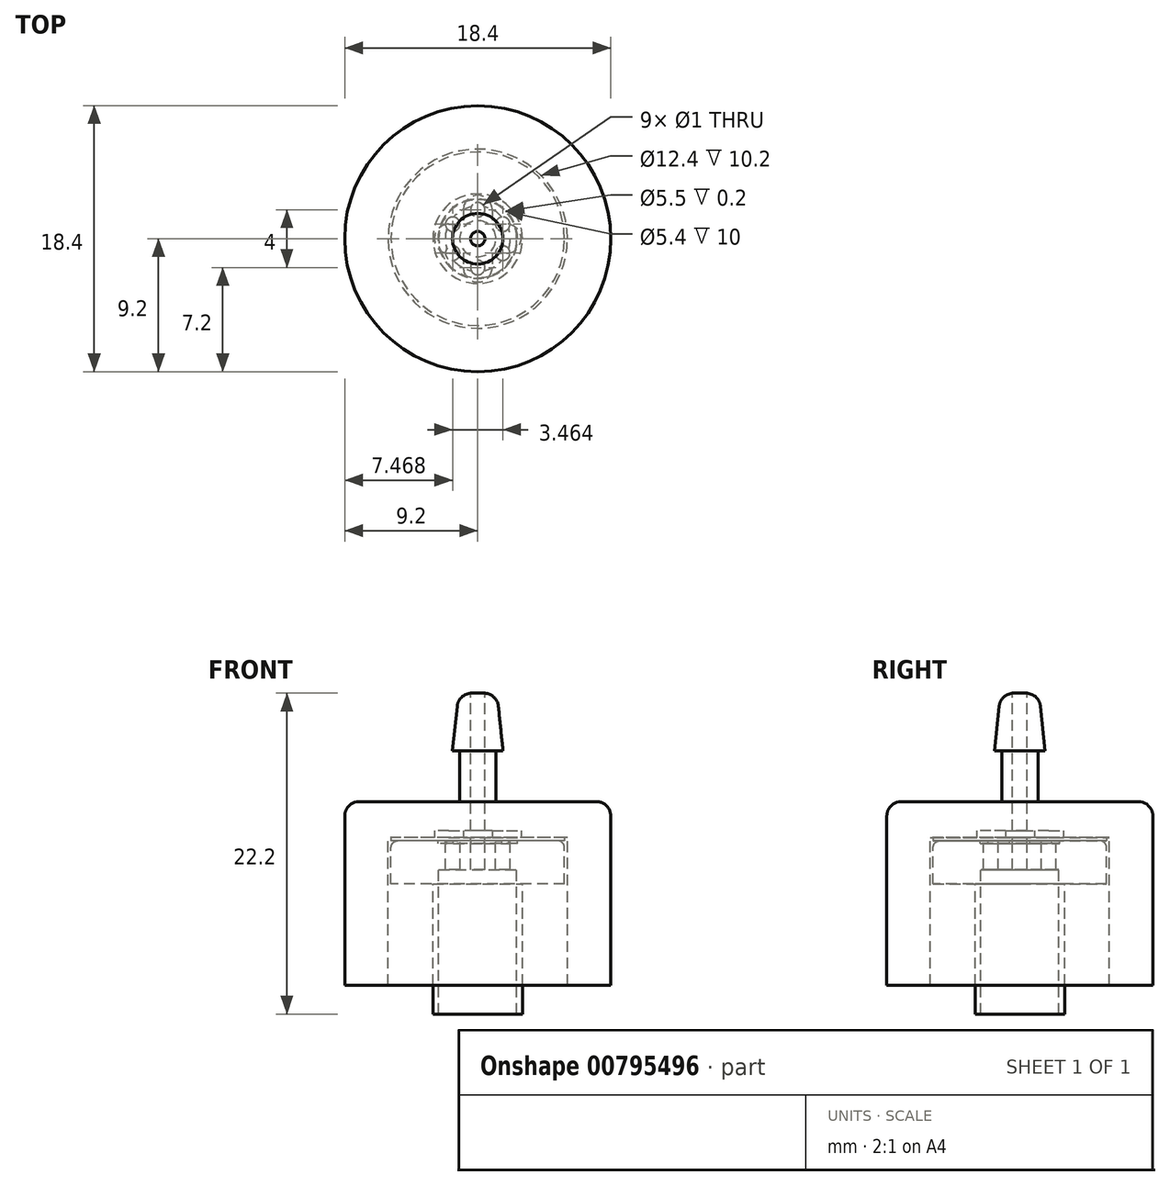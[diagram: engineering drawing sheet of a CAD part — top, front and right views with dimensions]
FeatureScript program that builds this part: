
annotation { "Feature Type Name" : "Feature", "Feature Type Description" : "" }
export const myFeature = defineFeature(function(context is Context, id is Id, definition is map)
    precondition{}
    {
        {
            var Q0;
            Q0=qCreatedBy(makeId("Top.planeOp"),FACE);
            var sketch = newSketch(context, id + "F0", { "sketchPlane" : qUnion([Q0])});
            skCircle(sketch, "E0", {"center": v(0, 0) * mm, "radius": 6 * mm});
            skCircle(sketch, "E1", {"center": v(0, 0) * mm, "radius": 3.1 * mm});
            skCircle(sketch, "E2", {"center": v(0, 2) * mm, "radius": 0.5 * mm});
            skCircle(sketch, "E3.1.0", {"center": v(-1.73, 1) * mm, "radius": 0.5 * mm});
            skCircle(sketch, "E3.2.0", {"center": v(-1.73, -1) * mm, "radius": 0.5 * mm});
            skCircle(sketch, "E3.3.0", {"center": v(0, -2) * mm, "radius": 0.5 * mm});
            skCircle(sketch, "E3.4.0", {"center": v(1.73, -1) * mm, "radius": 0.5 * mm});
            skCircle(sketch, "E3.5.0", {"center": v(1.73, 1) * mm, "radius": 0.5 * mm});
            skCircle(sketch, "E4", {"center": v(0, 0) * mm, "radius": 0.5 * mm});
            skSolve(sketch);
        }
        {
            var Q0;
            Q0=makeQuery(id+"F0.imprint","IMPRINT",FACE,{"disambiguationData":[TD([[makeQuery(id+"F0.imprint","IMPRINT",EDGE,{"derivedFrom":sQuery(id+"F0.wireOp",EDGE,"E0")}),1.0]])]});
            var Q1;
            Q1=makeQuery(id+"F0.imprint","IMPRINT",FACE,{"disambiguationData":[TD([[makeQuery(id+"F0.imprint","IMPRINT",EDGE,{"derivedFrom":sQuery(id+"F0.wireOp",EDGE,"E1")}),1.0]])]});
            extrude(context, id + "F1", {"entities" : qUnion([Q0, Q1]), "oppositeDirection" : true, "depth" : 2 * mm, "offsetDistance" : 25 * mm});
        }
        {
            var Q0;
            Q0=makeQuery(id+"F1.opExtrude","CAP_FACE",FACE,{"disambiguationData":[OSD([sQuery(id+"F0.wireOp",EDGE,"E0"),sQuery(id+"F0.wireOp",EDGE,"E2"),sQuery(id+"F0.wireOp",EDGE,"E3.1.0"),sQuery(id+"F0.wireOp",EDGE,"E3.2.0"),sQuery(id+"F0.wireOp",EDGE,"E3.3.0"),sQuery(id+"F0.wireOp",EDGE,"E3.4.0"),sQuery(id+"F0.wireOp",EDGE,"E3.5.0"),sQuery(id+"F0.wireOp",EDGE,"E4")])],"isStart":true});
            var sketch = newSketch(context, id + "F2", { "sketchPlane" : qUnion([Q0])});
            skCircle(sketch, "E5", {"center": v(0, 0) * mm, "radius": 2.75 * mm});
            skCircle(sketch, "E6", {"center": v(0, 0) * mm, "radius": 2.25 * mm});
            skSolve(sketch);
        }
        {
            var Q0;
            Q0=makeQuery(id+"F2.imprint","IMPRINT",FACE,{"disambiguationData":[TD([[makeQuery(id+"F2.imprint","IMPRINT",EDGE,{"derivedFrom":sQuery(id+"F2.wireOp",EDGE,"E5")}),1.0]])]});
            extrude(context, id + "F3", {"entities" : qUnion([Q0]), "operationType" : NewBodyOperationType.REMOVE, "oppositeDirection" : true, "depth" : 0.2 * mm, "offsetDistance" : 25 * mm});
        }
        {
            var Q0;
            Q0=makeQuery(id+"F1.opExtrude","CAP_FACE",FACE,{"disambiguationData":[OSD([sQuery(id+"F0.wireOp",EDGE,"E0")])],"isStart":false});
            var sketch = newSketch(context, id + "F4", { "sketchPlane" : qUnion([Q0])});
            skCircle(sketch, "E7.0", {"center": v(0, 0) * mm, "radius": 3.1 * mm});
            skCircle(sketch, "E7.1", {"center": v(0, 0) * mm, "radius": 6 * mm});
            skCircle(sketch, "E8", {"center": v(0, 0) * mm, "radius": 2.7 * mm});
            skSolve(sketch);
        }
        {
            var Q0;
            Q0=makeQuery(id+"F4.imprint","IMPRINT",FACE,{"disambiguationData":[TD([[makeQuery(id+"F4.imprint","IMPRINT",EDGE,{"derivedFrom":sQuery(id+"F4.wireOp",EDGE,"E7.0")}),-1.0]])]});
            extrude(context, id + "F5", {"entities" : qUnion([Q0]), "operationType" : NewBodyOperationType.ADD, "depth" : 1 * mm, "offsetDistance" : 25 * mm});
        }
        {
            var Q0;
            Q0=makeQuery(id+"F4.imprint","IMPRINT",FACE,{"disambiguationData":[TD([[makeQuery(id+"F4.imprint","IMPRINT",EDGE,{"derivedFrom":sQuery(id+"F4.wireOp",EDGE,"E7.0")}),1.0]])]});
            extrude(context, id + "F6", {"entities" : qUnion([Q0]), "operationType" : NewBodyOperationType.ADD, "depth" : 10 * mm, "offsetDistance" : 25 * mm});
        }
        {
            var Q0;
            Q0=makeQuery(id+"F0.imprint","IMPRINT",FACE,{"disambiguationData":[TD([[makeQuery(id+"F0.imprint","IMPRINT",EDGE,{"derivedFrom":sQuery(id+"F0.wireOp",EDGE,"E0")}),1.0]])]});
            cPlane(context, id + "F7", {"entities" : qUnion([Q0]), "cplaneType" : CPlaneType.OFFSET, "offset" : 0 * mm, "width" : 150 * mm, "height" : 150 * mm});
        }
        {
            var Q0;
            Q0=qCreatedBy(id+"F7.planeOp",FACE);
            var sketch = newSketch(context, id + "F8", { "sketchPlane" : qUnion([Q0])});
            skCircle(sketch, "E9", {"center": v(0, 0) * mm, "radius": 6.2 * mm});
            skCircle(sketch, "E10", {"center": v(0, 0) * mm, "radius": 9.2 * mm});
            skCircle(sketch, "E11.0", {"center": v(-1.73, 1) * mm, "radius": 0.5 * mm});
            skCircle(sketch, "E11.1", {"center": v(0, 2) * mm, "radius": 0.5 * mm});
            skCircle(sketch, "E11.2", {"center": v(1.73, 1) * mm, "radius": 0.5 * mm});
            skCircle(sketch, "E11.3", {"center": v(1.73, -1) * mm, "radius": 0.5 * mm});
            skCircle(sketch, "E11.4", {"center": v(0, -2) * mm, "radius": 0.5 * mm});
            skCircle(sketch, "E11.5", {"center": v(-1.73, -1) * mm, "radius": 0.5 * mm});
            skCircle(sketch, "E11.6", {"center": v(0, 0) * mm, "radius": 0.5 * mm});
            skCircle(sketch, "E12.0", {"center": v(0, 0) * mm, "radius": 6 * mm});
            skSolve(sketch);
        }
        {
            var Q0;
            Q0=makeQuery(id+"F8.imprint","IMPRINT",FACE,{"disambiguationData":[TD([[makeQuery(id+"F8.imprint","IMPRINT",EDGE,{"derivedFrom":sQuery(id+"F8.wireOp",EDGE,"E11.0")}),-1.0]])]});
            var Q1;
            Q1=makeQuery(id+"F8.imprint","IMPRINT",FACE,{"disambiguationData":[TD([[makeQuery(id+"F8.imprint","IMPRINT",EDGE,{"derivedFrom":sQuery(id+"F8.wireOp",EDGE,"E11.0")}),1.0]])]});
            var Q2;
            Q2=makeQuery(id+"F8.imprint","IMPRINT",FACE,{"disambiguationData":[TD([[makeQuery(id+"F8.imprint","IMPRINT",EDGE,{"derivedFrom":sQuery(id+"F8.wireOp",EDGE,"E11.1")}),1.0]])]});
            var Q3;
            Q3=makeQuery(id+"F8.imprint","IMPRINT",FACE,{"disambiguationData":[TD([[makeQuery(id+"F8.imprint","IMPRINT",EDGE,{"derivedFrom":sQuery(id+"F8.wireOp",EDGE,"E11.2")}),1.0]])]});
            var Q4;
            Q4=makeQuery(id+"F8.imprint","IMPRINT",FACE,{"disambiguationData":[TD([[makeQuery(id+"F8.imprint","IMPRINT",EDGE,{"derivedFrom":sQuery(id+"F8.wireOp",EDGE,"E11.3")}),1.0]])]});
            var Q5;
            Q5=makeQuery(id+"F8.imprint","IMPRINT",FACE,{"disambiguationData":[TD([[makeQuery(id+"F8.imprint","IMPRINT",EDGE,{"derivedFrom":sQuery(id+"F8.wireOp",EDGE,"E11.4")}),1.0]])]});
            var Q6;
            Q6=makeQuery(id+"F8.imprint","IMPRINT",FACE,{"disambiguationData":[TD([[makeQuery(id+"F8.imprint","IMPRINT",EDGE,{"derivedFrom":sQuery(id+"F8.wireOp",EDGE,"E11.5")}),1.0]])]});
            var Q7;
            Q7=makeQuery(id+"F8.imprint","IMPRINT",FACE,{"disambiguationData":[TD([[makeQuery(id+"F8.imprint","IMPRINT",EDGE,{"derivedFrom":sQuery(id+"F8.wireOp",EDGE,"E11.6")}),1.0]])]});
            extrude(context, id + "F9", {"entities" : qUnion([Q0, Q1, Q2, Q3, Q4, Q5, Q6, Q7]), "depth" : 0.2 * mm, "offsetDistance" : 25 * mm});
        }
        {
            var Q0;
            Q0 = qSketchRegion(id + "F8", true);
            extrude(context, id + "F10", {"entities" : qUnion([Q0]), "oppositeDirection" : true, "depth" : 10 * mm, "offsetDistance" : 25 * mm});
        }
        {
            var Q0;
            Q0=makeQuery(id+"F10.opExtrude","CAP_FACE",FACE,{"disambiguationData":[OSD([sQuery(id+"F8.wireOp",EDGE,"E9"),sQuery(id+"F8.wireOp",EDGE,"E10")])],"isStart":true});
            extrude(context, id + "F11", {"entities" : qUnion([Q0]), "operationType" : NewBodyOperationType.ADD, "depth" : 0.2 * mm, "offsetDistance" : 25 * mm});
        }
        {
            var Q0;
            Q0=makeQuery(id+"F11.opExtrude","CAP_FACE",FACE,{"disambiguationData":[OSD([sQuery(id+"F8.wireOp",EDGE,"E9"),sQuery(id+"F8.wireOp",EDGE,"E10")])],"isStart":false});
            var sketch = newSketch(context, id + "F12", { "sketchPlane" : qUnion([Q0])});
            skLineSegment(sketch, "E13.bottom", {"start": v(-2, 1) * mm, "end": v(2, 1) * mm});
            skLineSegment(sketch, "E13.top", {"start": v(-2, -1) * mm, "end": v(2, -1) * mm});
            skLineSegment(sketch, "E13.left", {"start": v(-3, 0) * mm, "end": v(-3, 0) * mm});
            skLineSegment(sketch, "E13.right", {"start": v(3, 0) * mm, "end": v(3, 0) * mm});
            skLineSegment(sketch, "E14.bottom", {"start": v(0, 3) * mm, "end": v(0, 3) * mm});
            skLineSegment(sketch, "E14.top", {"start": v(0, -3) * mm, "end": v(0, -3) * mm});
            skLineSegment(sketch, "E14.left", {"start": v(-1, 2) * mm, "end": v(-1, -2) * mm});
            skLineSegment(sketch, "E14.right", {"start": v(1, 2) * mm, "end": v(1, -2) * mm});
            skLineSegment(sketch, "E15", {"start": v(-4.57, 0) * mm, "end": v(4.82, 0) * mm, "construction": true});
            skLineSegment(sketch, "E16", {"start": v(0, 3.73) * mm, "end": v(0, -3.96) * mm, "construction": true});
            skPoint(sketch, "E17.visualSharp", {"position": v(-3, -1) * mm});
            skArc(sketch, "E17.filletArc", {"start": v(-3, 0) * mm, "mid": v(-2.7, -0.7) * mm, "end": v(-2, -1) * mm});
            skPoint(sketch, "E18.visualSharp", {"position": v(-3, 1) * mm});
            skArc(sketch, "E18.filletArc", {"start": v(-2, 1) * mm, "mid": v(-2.7, 0.7) * mm, "end": v(-3, 0) * mm});
            skPoint(sketch, "E19.visualSharp", {"position": v(-1, 3) * mm});
            skArc(sketch, "E19.filletArc", {"start": v(0, 3) * mm, "mid": v(-0.7, 2.7) * mm, "end": v(-1, 2) * mm});
            skPoint(sketch, "E20.visualSharp", {"position": v(1, 3) * mm});
            skArc(sketch, "E20.filletArc", {"start": v(1, 2) * mm, "mid": v(0.7, 2.7) * mm, "end": v(0, 3) * mm});
            skPoint(sketch, "E21.visualSharp", {"position": v(3, 1) * mm});
            skArc(sketch, "E21.filletArc", {"start": v(3, 0) * mm, "mid": v(2.7, 0.7) * mm, "end": v(2, 1) * mm});
            skPoint(sketch, "E22.visualSharp", {"position": v(3, -1) * mm});
            skArc(sketch, "E22.filletArc", {"start": v(2, -1) * mm, "mid": v(2.7, -0.7) * mm, "end": v(3, 0) * mm});
            skPoint(sketch, "E23.visualSharp", {"position": v(1, -3) * mm});
            skArc(sketch, "E23.filletArc", {"start": v(0, -3) * mm, "mid": v(0.7, -2.7) * mm, "end": v(1, -2) * mm});
            skPoint(sketch, "E24.visualSharp", {"position": v(-1, -3) * mm});
            skArc(sketch, "E24.filletArc", {"start": v(-1, -2) * mm, "mid": v(-0.7, -2.7) * mm, "end": v(0, -3) * mm});
            skSolve(sketch);
        }
        {
            var Q0;
            Q0=makeQuery(id+"F12.imprint","IMPRINT",FACE,{"disambiguationData":[TD([[makeQuery(id+"F12.imprint","IMPRINT",EDGE,{"derivedFrom":makeQuery(id+"F11.opExtrude","CAP_EDGE",EDGE,{"disambiguationData":[OSD([sQuery(id+"F8.wireOp",EDGE,"E9")])],"isStart":false})}),-1.0]])]});
            var Q1;
            {var subQ0=sQuery(id+"F12.wireOp",EDGE,"E17.filletArc");Q1=makeQuery(id+"F12.imprint","IMPRINT",FACE,{"disambiguationData":[TD([[makeQuery(id+"F12.imprint","IMPRINT",EDGE,{"derivedFrom":subQ0}),-1.0]])]});}
            extrude(context, id + "F13", {"entities" : qUnion([Q0, Q1]), "operationType" : NewBodyOperationType.ADD, "depth" : 0.5 * mm, "offsetDistance" : 25 * mm});
        }
        {
            var Q0;
            Q0=makeQuery(id+"F13.opExtrude","CAP_FACE",FACE,{"disambiguationData":[OSD([sQuery(id+"F8.wireOp",EDGE,"E10"),sQuery(id+"F12.wireOp",EDGE,"E13.bottom"),sQuery(id+"F12.wireOp",EDGE,"E13.top"),sQuery(id+"F12.wireOp",EDGE,"E13.left"),sQuery(id+"F12.wireOp",EDGE,"E13.right"),sQuery(id+"F12.wireOp",EDGE,"E14.bottom"),sQuery(id+"F12.wireOp",EDGE,"E14.top"),sQuery(id+"F12.wireOp",EDGE,"E14.left"),sQuery(id+"F12.wireOp",EDGE,"E14.right")])],"isStart":false});
            var sketch = newSketch(context, id + "F14", { "sketchPlane" : qUnion([Q0])});
            skCircle(sketch, "E25.0", {"center": v(0, 0) * mm, "radius": 9.2 * mm});
            skSolve(sketch);
        }
        {
            var Q0;
            Q0=makeQuery(id+"F14.imprint","IMPRINT",FACE,{"disambiguationData":[TD([[makeQuery(id+"F14.imprint","IMPRINT",EDGE,{"derivedFrom":sQuery(id+"F14.wireOp",EDGE,"E25.0")}),1.0]])]});
            var Q1;
            {var subQ8=sQuery(id+"F12.wireOp",EDGE,"E13.left");Q1=makeQuery(id+"F14.imprint","IMPRINT",FACE,{"disambiguationData":[TD([[makeQuery(id+"F14.imprint","IMPRINT",EDGE,{"derivedFrom":makeQuery(id+"F13.opExtrude","CAP_EDGE",EDGE,{"disambiguationData":[OSD([subQ8])],"isStart":false})}),1.0]])]});}
            var Q2;
            {var subQ2=sQuery(id+"F12.wireOp",EDGE,"E18.filletArc");var subQ3=sQuery(id+"F12.wireOp",EDGE,"E17.filletArc");Q2=makeQuery(id+"F14.imprint","IMPRINT",FACE,{"disambiguationData":[TD([[makeQuery(id+"F14.imprint","IMPRINT",EDGE,{"derivedFrom":makeQuery(id+"F13.opExtrude","CAP_EDGE",EDGE,{"disambiguationData":[OSD([subQ3,subQ2])],"isStart":false})}),1.0]])]});}
            extrude(context, id + "F15", {"entities" : qUnion([Q0, Q1, Q2]), "operationType" : NewBodyOperationType.ADD, "depth" : 2 * mm, "offsetDistance" : 25 * mm});
        }
        {
            var Q0;
            Q0=makeQuery(id+"F15.opExtrude","CAP_FACE",FACE,{"disambiguationData":[OSD([sQuery(id+"F14.wireOp",EDGE,"E25.0")])],"isStart":false});
            var sketch = newSketch(context, id + "F16", { "sketchPlane" : qUnion([Q0])});
            skPoint(sketch, "E26.0", {"position": v(0, 0) * mm});
            skCircle(sketch, "E27", {"center": v(0, 0) * mm, "radius": 1.25 * mm});
            skSolve(sketch);
        }
        {
            var Q0;
            Q0=makeQuery(id+"F16.imprint","IMPRINT",FACE,{"disambiguationData":[TD([[makeQuery(id+"F16.imprint","IMPRINT",EDGE,{"derivedFrom":sQuery(id+"F16.wireOp",EDGE,"E27")}),1.0]])]});
            var Q1;
            Q1=sQuery(id+"F16.wireOp",EDGE,"E27");
            extrude(context, id + "F17", {"entities" : qUnion([Q0]), "operationType" : NewBodyOperationType.ADD, "surfaceEntities" : qUnion([Q1]), "depth" : 3.5 * mm, "offsetDistance" : 25 * mm});
        }
        {
            var Q0;
            Q0=makeQuery(id+"F17.opExtrude","CAP_FACE",FACE,{"disambiguationData":[OSD([sQuery(id+"F16.wireOp",EDGE,"E27")])],"isStart":false});
            var sketch = newSketch(context, id + "F18", { "sketchPlane" : qUnion([Q0])});
            skCircle(sketch, "E28.0", {"center": v(0, 0) * mm, "radius": 1.25 * mm});
            skCircle(sketch, "E29", {"center": v(0, 0) * mm, "radius": 1.75 * mm});
            skSolve(sketch);
        }
        {
            var Q0;
            Q0=makeQuery(id+"F18.imprint","IMPRINT",FACE,{"disambiguationData":[TD([[makeQuery(id+"F18.imprint","IMPRINT",EDGE,{"derivedFrom":sQuery(id+"F18.wireOp",EDGE,"E28.0")}),-1.0]])]});
            var Q1;
            Q1=makeQuery(id+"F18.imprint","IMPRINT",FACE,{"disambiguationData":[TD([[makeQuery(id+"F18.imprint","IMPRINT",EDGE,{"derivedFrom":sQuery(id+"F18.wireOp",EDGE,"E28.0")}),1.0]])]});
            extrude(context, id + "F19", {"entities" : qUnion([Q0, Q1]), "operationType" : NewBodyOperationType.ADD, "depth" : 4 * mm, "offsetDistance" : 25 * mm, "hasDraft" : true, "draftAngle" : 6 * degree, "draftPullDirection" : true});
        }
        {
            var Q0;
            Q0=makeQuery(id+"F19.opExtrude","CAP_FACE",FACE,{"disambiguationData":[OSD([sQuery(id+"F18.wireOp",EDGE,"E29")])],"isStart":false});
            var sketch = newSketch(context, id + "F20", { "sketchPlane" : qUnion([Q0])});
            skPoint(sketch, "E30.0", {"position": v(0, 0) * mm});
            skCircle(sketch, "E31", {"center": v(0, 0) * mm, "radius": 0.5 * mm});
            skSolve(sketch);
        }
        {
            var Q0;
            Q0=makeQuery(id+"F20.imprint","IMPRINT",FACE,{"disambiguationData":[TD([[makeQuery(id+"F20.imprint","IMPRINT",EDGE,{"derivedFrom":sQuery(id+"F20.wireOp",EDGE,"E31")}),1.0]])]});
            extrude(context, id + "F21", {"entities" : qUnion([Q0]), "operationType" : NewBodyOperationType.REMOVE, "oppositeDirection" : true, "depth" : 25 * mm, "offsetDistance" : 25 * mm});
        }
        {
            var Q0;
            Q0=makeQuery(id+"F15.opExtrude","CAP_EDGE",EDGE,{"disambiguationData":[OSD([sQuery(id+"F14.wireOp",EDGE,"E25.0")])],"isStart":false});
            var Q1;
            Q1=makeQuery(id+"F19.opExtrude","CAP_EDGE",EDGE,{"disambiguationData":[OSD([sQuery(id+"F18.wireOp",EDGE,"E29")])],"isStart":false});
            var Q2;
            Q2=makeQuery(id+"F17.opExtrude","CAP_EDGE",EDGE,{"disambiguationData":[OSD([sQuery(id+"F16.wireOp",EDGE,"E27")])],"isStart":true});
            fillet(context, id + "F22", {"entities" : qUnion([Q0, Q1, Q2]), "radius" : 1 * mm, "tangentPropagation" : true, "allowEdgeOverflow" : false});
        }
        {
            var Q0;
            Q0=makeQuery(id+"F1.opExtrude","CAP_EDGE",EDGE,{"disambiguationData":[OSD([sQuery(id+"F0.wireOp",EDGE,"E0")])],"isStart":true});
            fillet(context, id + "F23", {"entities" : qUnion([Q0]), "radius" : 0.5 * mm, "tangentPropagation" : true, "allowEdgeOverflow" : false});
        }
    });
